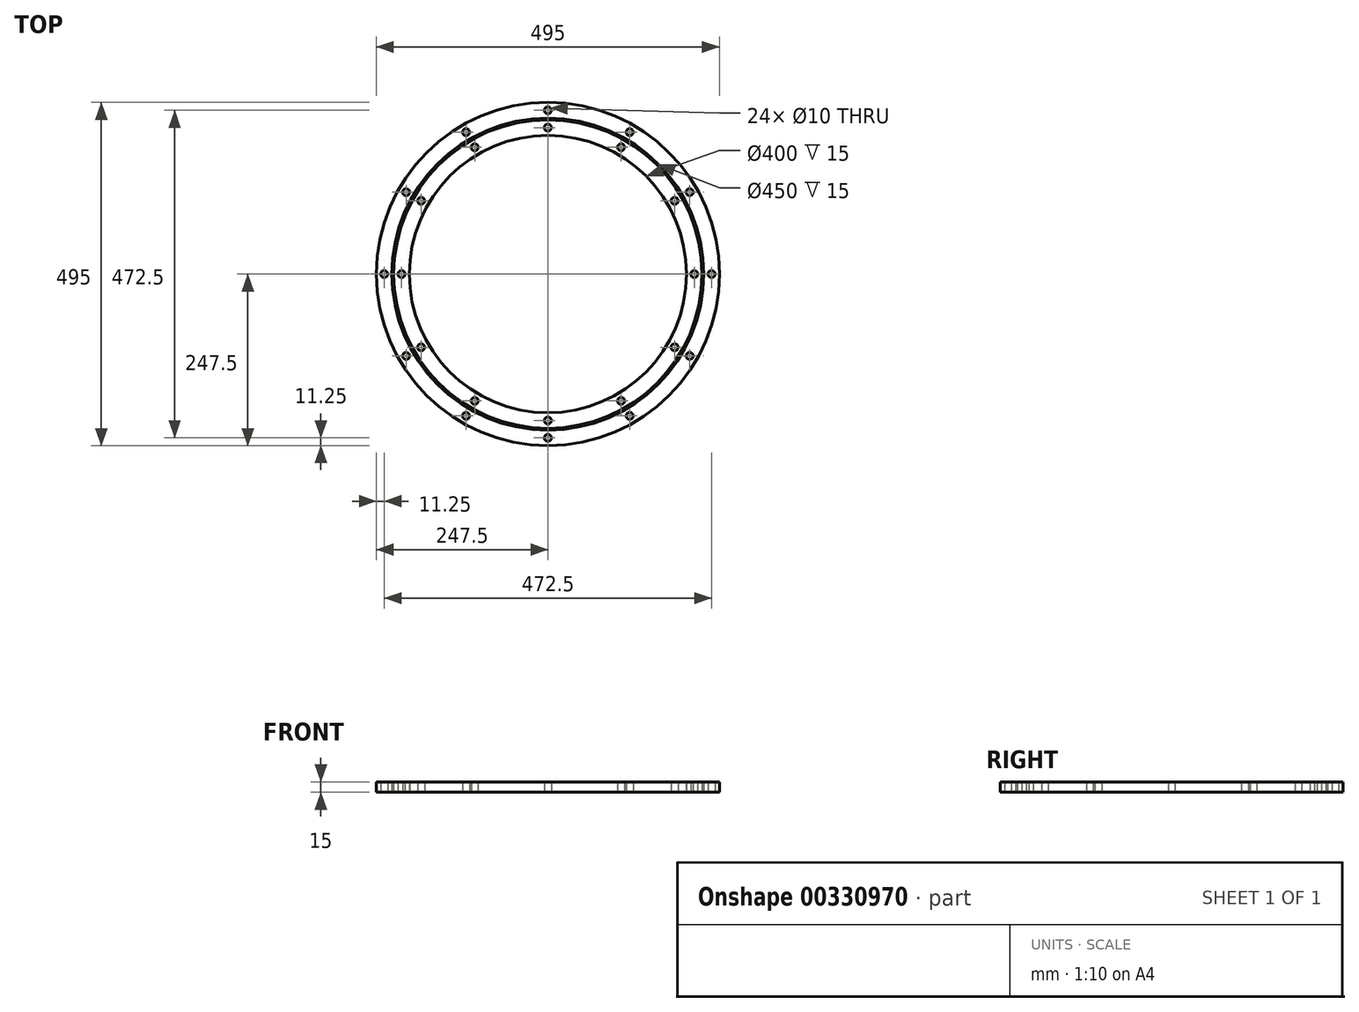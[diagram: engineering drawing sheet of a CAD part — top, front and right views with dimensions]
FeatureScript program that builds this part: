
annotation { "Feature Type Name" : "Feature", "Feature Type Description" : "" }
export const myFeature = defineFeature(function(context is Context, id is Id, definition is map)
    precondition{}
    {
        {
            var Q0;
            Q0=qCreatedBy(makeId("Top.planeOp"),FACE);
            var sketch = newSketch(context, id + "F0", { "sketchPlane" : qUnion([Q0])});
            skCircle(sketch, "E0", {"center": v(0, 0) * mm, "radius": 200 * mm});
            skCircle(sketch, "E1", {"center": v(0, 0) * mm, "radius": 225 * mm});
            skCircle(sketch, "E2", {"center": v(0, 0) * mm, "radius": 222.5 * mm});
            skCircle(sketch, "E3", {"center": v(0, 0) * mm, "radius": 247.5 * mm});
            skLineSegment(sketch, "E4", {"start": v(0, 225) * mm, "end": v(0, 236.25) * mm});
            skCircle(sketch, "E5", {"center": v(0, 236.25) * mm, "radius": 5 * mm});
            skCircle(sketch, "E6.1.0", {"center": v(118.12, 204.6) * mm, "radius": 5 * mm});
            skCircle(sketch, "E6.2.0", {"center": v(204.6, 118.13) * mm, "radius": 5 * mm});
            skLineSegment(sketch, "E6.anchor1", {"start": v(0, 0) * mm, "end": v(0, 236.25) * mm, "construction": true});
            skLineSegment(sketch, "E6.anchor2", {"start": v(0, 0) * mm, "end": v(204.6, 118.13) * mm, "construction": true});
            skCircle(sketch, "E7.1.0", {"center": v(236.25, 0) * mm, "radius": 5 * mm});
            skCircle(sketch, "E7.2.0", {"center": v(204.6, -118.12) * mm, "radius": 5 * mm});
            skLineSegment(sketch, "E7.anchor2", {"start": v(0, 0) * mm, "end": v(204.6, -118.12) * mm, "construction": true});
            skCircle(sketch, "E8.1.0", {"center": v(118.13, -204.6) * mm, "radius": 5 * mm});
            skCircle(sketch, "E8.2.0", {"center": v(0, -236.25) * mm, "radius": 5 * mm});
            skLineSegment(sketch, "E8.anchor2", {"start": v(0, 0) * mm, "end": v(0, -236.25) * mm, "construction": true});
            skCircle(sketch, "E9.1.0", {"center": v(-118.12, -204.6) * mm, "radius": 5 * mm});
            skCircle(sketch, "E9.2.0", {"center": v(-204.6, -118.13) * mm, "radius": 5 * mm});
            skLineSegment(sketch, "E9.anchor2", {"start": v(0, 0) * mm, "end": v(-204.6, -118.13) * mm, "construction": true});
            skCircle(sketch, "E10.1.0", {"center": v(-236.25, 0) * mm, "radius": 5 * mm});
            skCircle(sketch, "E10.2.0", {"center": v(-204.6, 118.12) * mm, "radius": 5 * mm});
            skLineSegment(sketch, "E10.anchor2", {"start": v(0, 0) * mm, "end": v(-204.6, 118.12) * mm, "construction": true});
            skCircle(sketch, "E11.1.0", {"center": v(-118.13, 204.6) * mm, "radius": 5 * mm});
            skLineSegment(sketch, "E12", {"start": v(0, 200) * mm, "end": v(0, 211.25) * mm});
            skCircle(sketch, "E13", {"center": v(0, 211.25) * mm, "radius": 5 * mm});
            skCircle(sketch, "E14.1.0", {"center": v(105.62, 182.95) * mm, "radius": 5 * mm});
            skCircle(sketch, "E14.2.0", {"center": v(182.95, 105.63) * mm, "radius": 5 * mm});
            skLineSegment(sketch, "E14.anchor1", {"start": v(0, 0) * mm, "end": v(0, 211.25) * mm, "construction": true});
            skLineSegment(sketch, "E14.anchor2", {"start": v(0, 0) * mm, "end": v(182.95, 105.63) * mm, "construction": true});
            skCircle(sketch, "E15.1.0", {"center": v(211.25, 0) * mm, "radius": 5 * mm});
            skCircle(sketch, "E15.2.0", {"center": v(182.95, -105.62) * mm, "radius": 5 * mm});
            skLineSegment(sketch, "E15.anchor2", {"start": v(0, 0) * mm, "end": v(182.95, -105.62) * mm, "construction": true});
            skCircle(sketch, "E16.1.0", {"center": v(105.63, -182.95) * mm, "radius": 5 * mm});
            skCircle(sketch, "E16.2.0", {"center": v(0, -211.25) * mm, "radius": 5 * mm});
            skLineSegment(sketch, "E16.anchor2", {"start": v(0, 0) * mm, "end": v(0, -211.25) * mm, "construction": true});
            skCircle(sketch, "E17.1.0", {"center": v(-105.62, -182.95) * mm, "radius": 5 * mm});
            skCircle(sketch, "E17.2.0", {"center": v(-182.95, -105.63) * mm, "radius": 5 * mm});
            skLineSegment(sketch, "E17.anchor2", {"start": v(0, 0) * mm, "end": v(-182.95, -105.63) * mm, "construction": true});
            skCircle(sketch, "E18.1.0", {"center": v(-211.25, 0) * mm, "radius": 5 * mm});
            skCircle(sketch, "E18.2.0", {"center": v(-182.95, 105.62) * mm, "radius": 5 * mm});
            skLineSegment(sketch, "E18.anchor2", {"start": v(0, 0) * mm, "end": v(-182.95, 105.62) * mm, "construction": true});
            skCircle(sketch, "E19.1.0", {"center": v(-105.63, 182.95) * mm, "radius": 5 * mm});
            skSolve(sketch);
        }
        {
            var Q0;
            Q0=makeQuery(id+"F0.imprint","IMPRINT",FACE,{"disambiguationData":[TD([[makeQuery(id+"F0.imprint","IMPRINT",EDGE,{"derivedFrom":sQuery(id+"F0.wireOp",EDGE,"E0")}),-1.0]])]});
            var Q1;
            Q1=makeQuery(id+"F0.imprint","IMPRINT",FACE,{"disambiguationData":[TD([[makeQuery(id+"F0.imprint","IMPRINT",EDGE,{"derivedFrom":sQuery(id+"F0.wireOp",EDGE,"E1")}),-1.0]])]});
            extrude(context, id + "F1", {"entities" : qUnion([Q0, Q1]), "depth" : 15 * mm});
        }
    });
